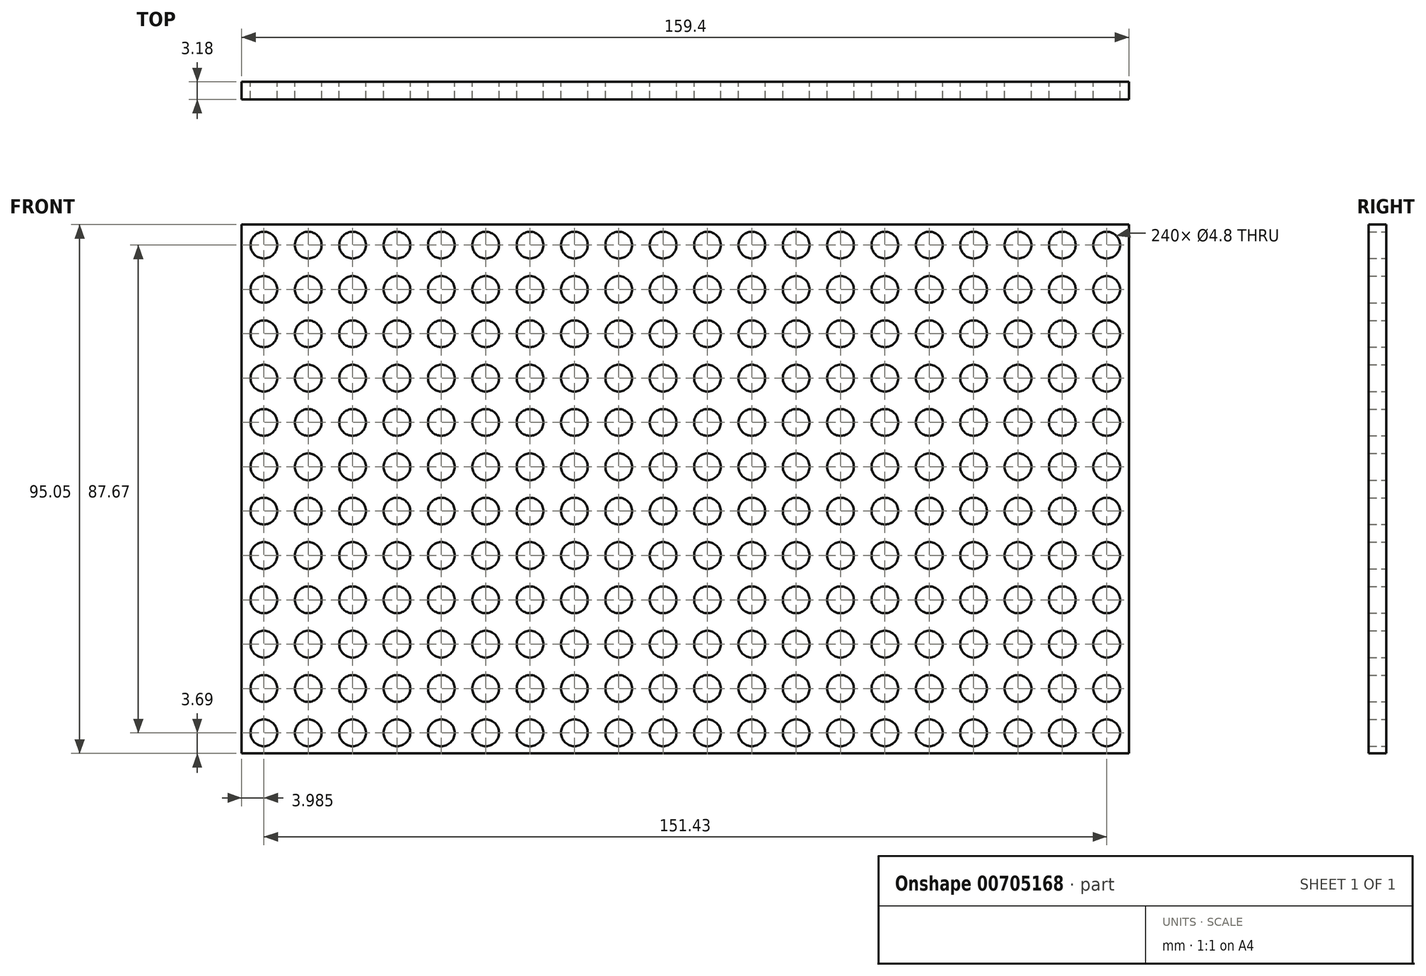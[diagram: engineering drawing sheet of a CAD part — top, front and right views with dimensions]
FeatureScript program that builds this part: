
annotation { "Feature Type Name" : "Feature", "Feature Type Description" : "" }
export const myFeature = defineFeature(function(context is Context, id is Id, definition is map)
    precondition{}
    {
        {
            var Q0;
            Q0=qCreatedBy(makeId("Front.planeOp"),FACE);
            var sketch = newSketch(context, id + "F0", { "sketchPlane" : qUnion([Q0])});
            skLineSegment(sketch, "E0.bottom", {"start": v(0, 0) * mm, "end": v(159.4, 0) * mm});
            skLineSegment(sketch, "E0.top", {"start": v(0, -95.05) * mm, "end": v(159.4, -95.05) * mm});
            skLineSegment(sketch, "E0.left", {"start": v(0, 0) * mm, "end": v(0, -95.05) * mm});
            skLineSegment(sketch, "E0.right", {"start": v(159.4, 0) * mm, "end": v(159.4, -95.05) * mm});
            skCircle(sketch, "E1", {"center": v(3.98, -3.69) * mm, "radius": 2.4 * mm});
            skCircle(sketch, "E2", {"center": v(11.95, -3.69) * mm, "radius": 2.4 * mm});
            skCircle(sketch, "E3.1.0.0", {"center": v(19.92, -3.69) * mm, "radius": 2.4 * mm});
            skCircle(sketch, "E3.2.0.0", {"center": v(27.9, -3.69) * mm, "radius": 2.4 * mm});
            skCircle(sketch, "E3.3.0.0", {"center": v(35.86, -3.69) * mm, "radius": 2.4 * mm});
            skCircle(sketch, "E3.4.0.0", {"center": v(43.83, -3.69) * mm, "radius": 2.4 * mm});
            skCircle(sketch, "E3.5.0.0", {"center": v(51.8, -3.69) * mm, "radius": 2.4 * mm});
            skCircle(sketch, "E3.6.0.0", {"center": v(59.77, -3.69) * mm, "radius": 2.4 * mm});
            skCircle(sketch, "E3.7.0.0", {"center": v(67.74, -3.69) * mm, "radius": 2.4 * mm});
            skCircle(sketch, "E3.8.0.0", {"center": v(75.71, -3.69) * mm, "radius": 2.4 * mm});
            skCircle(sketch, "E3.9.0.0", {"center": v(83.68, -3.69) * mm, "radius": 2.4 * mm});
            skCircle(sketch, "E3.10.0.0", {"center": v(91.65, -3.69) * mm, "radius": 2.4 * mm});
            skCircle(sketch, "E3.11.0.0", {"center": v(99.62, -3.69) * mm, "radius": 2.4 * mm});
            skCircle(sketch, "E3.12.0.0", {"center": v(107.6, -3.69) * mm, "radius": 2.4 * mm});
            skCircle(sketch, "E3.13.0.0", {"center": v(115.56, -3.69) * mm, "radius": 2.4 * mm});
            skCircle(sketch, "E3.14.0.0", {"center": v(123.53, -3.69) * mm, "radius": 2.4 * mm});
            skCircle(sketch, "E3.15.0.0", {"center": v(131.5, -3.69) * mm, "radius": 2.4 * mm});
            skCircle(sketch, "E3.16.0.0", {"center": v(139.47, -3.69) * mm, "radius": 2.4 * mm});
            skCircle(sketch, "E3.17.0.0", {"center": v(147.44, -3.69) * mm, "radius": 2.4 * mm});
            skCircle(sketch, "E3.18.0.0", {"center": v(155.41, -3.69) * mm, "radius": 2.4 * mm});
            skLineSegment(sketch, "E3.direction1", {"start": v(11.95, -3.69) * mm, "end": v(19.92, -3.69) * mm, "construction": true});
            skCircle(sketch, "E4.0.1.0", {"center": v(3.98, -11.66) * mm, "radius": 2.4 * mm});
            skCircle(sketch, "E4.0.1.1", {"center": v(11.95, -11.66) * mm, "radius": 2.4 * mm});
            skCircle(sketch, "E4.0.1.2", {"center": v(19.92, -11.66) * mm, "radius": 2.4 * mm});
            skCircle(sketch, "E4.0.1.3", {"center": v(27.9, -11.66) * mm, "radius": 2.4 * mm});
            skCircle(sketch, "E4.0.1.4", {"center": v(35.86, -11.66) * mm, "radius": 2.4 * mm});
            skCircle(sketch, "E4.0.1.5", {"center": v(43.83, -11.66) * mm, "radius": 2.4 * mm});
            skCircle(sketch, "E4.0.1.6", {"center": v(51.8, -11.66) * mm, "radius": 2.4 * mm});
            skCircle(sketch, "E4.0.1.7", {"center": v(155.41, -11.66) * mm, "radius": 2.4 * mm});
            skCircle(sketch, "E4.0.1.8", {"center": v(147.44, -11.66) * mm, "radius": 2.4 * mm});
            skCircle(sketch, "E4.0.1.9", {"center": v(139.47, -11.66) * mm, "radius": 2.4 * mm});
            skCircle(sketch, "E4.0.1.10", {"center": v(131.5, -11.66) * mm, "radius": 2.4 * mm});
            skCircle(sketch, "E4.0.1.11", {"center": v(123.53, -11.66) * mm, "radius": 2.4 * mm});
            skCircle(sketch, "E4.0.1.12", {"center": v(115.56, -11.66) * mm, "radius": 2.4 * mm});
            skCircle(sketch, "E4.0.1.13", {"center": v(107.6, -11.66) * mm, "radius": 2.4 * mm});
            skCircle(sketch, "E4.0.1.14", {"center": v(99.62, -11.66) * mm, "radius": 2.4 * mm});
            skCircle(sketch, "E4.0.1.15", {"center": v(91.65, -11.66) * mm, "radius": 2.4 * mm});
            skCircle(sketch, "E4.0.1.16", {"center": v(83.68, -11.66) * mm, "radius": 2.4 * mm});
            skCircle(sketch, "E4.0.1.17", {"center": v(75.71, -11.66) * mm, "radius": 2.4 * mm});
            skCircle(sketch, "E4.0.1.18", {"center": v(67.74, -11.66) * mm, "radius": 2.4 * mm});
            skCircle(sketch, "E4.0.1.19", {"center": v(59.77, -11.66) * mm, "radius": 2.4 * mm});
            skCircle(sketch, "E4.0.2.0", {"center": v(3.98, -19.63) * mm, "radius": 2.4 * mm});
            skCircle(sketch, "E4.0.2.1", {"center": v(11.95, -19.63) * mm, "radius": 2.4 * mm});
            skCircle(sketch, "E4.0.2.2", {"center": v(19.92, -19.63) * mm, "radius": 2.4 * mm});
            skCircle(sketch, "E4.0.2.3", {"center": v(27.9, -19.63) * mm, "radius": 2.4 * mm});
            skCircle(sketch, "E4.0.2.4", {"center": v(35.86, -19.63) * mm, "radius": 2.4 * mm});
            skCircle(sketch, "E4.0.2.5", {"center": v(43.83, -19.63) * mm, "radius": 2.4 * mm});
            skCircle(sketch, "E4.0.2.6", {"center": v(51.8, -19.63) * mm, "radius": 2.4 * mm});
            skCircle(sketch, "E4.0.2.7", {"center": v(155.41, -19.63) * mm, "radius": 2.4 * mm});
            skCircle(sketch, "E4.0.2.8", {"center": v(147.44, -19.63) * mm, "radius": 2.4 * mm});
            skCircle(sketch, "E4.0.2.9", {"center": v(139.47, -19.63) * mm, "radius": 2.4 * mm});
            skCircle(sketch, "E4.0.2.10", {"center": v(131.5, -19.63) * mm, "radius": 2.4 * mm});
            skCircle(sketch, "E4.0.2.11", {"center": v(123.53, -19.63) * mm, "radius": 2.4 * mm});
            skCircle(sketch, "E4.0.2.12", {"center": v(115.56, -19.63) * mm, "radius": 2.4 * mm});
            skCircle(sketch, "E4.0.2.13", {"center": v(107.6, -19.63) * mm, "radius": 2.4 * mm});
            skCircle(sketch, "E4.0.2.14", {"center": v(99.62, -19.63) * mm, "radius": 2.4 * mm});
            skCircle(sketch, "E4.0.2.15", {"center": v(91.65, -19.63) * mm, "radius": 2.4 * mm});
            skCircle(sketch, "E4.0.2.16", {"center": v(83.68, -19.63) * mm, "radius": 2.4 * mm});
            skCircle(sketch, "E4.0.2.17", {"center": v(75.71, -19.63) * mm, "radius": 2.4 * mm});
            skCircle(sketch, "E4.0.2.18", {"center": v(67.74, -19.63) * mm, "radius": 2.4 * mm});
            skCircle(sketch, "E4.0.2.19", {"center": v(59.77, -19.63) * mm, "radius": 2.4 * mm});
            skCircle(sketch, "E4.0.3.0", {"center": v(3.98, -27.6) * mm, "radius": 2.4 * mm});
            skCircle(sketch, "E4.0.3.1", {"center": v(11.95, -27.6) * mm, "radius": 2.4 * mm});
            skCircle(sketch, "E4.0.3.2", {"center": v(19.92, -27.6) * mm, "radius": 2.4 * mm});
            skCircle(sketch, "E4.0.3.3", {"center": v(27.9, -27.6) * mm, "radius": 2.4 * mm});
            skCircle(sketch, "E4.0.3.4", {"center": v(35.86, -27.6) * mm, "radius": 2.4 * mm});
            skCircle(sketch, "E4.0.3.5", {"center": v(43.83, -27.6) * mm, "radius": 2.4 * mm});
            skCircle(sketch, "E4.0.3.6", {"center": v(51.8, -27.6) * mm, "radius": 2.4 * mm});
            skCircle(sketch, "E4.0.3.7", {"center": v(155.41, -27.6) * mm, "radius": 2.4 * mm});
            skCircle(sketch, "E4.0.3.8", {"center": v(147.44, -27.6) * mm, "radius": 2.4 * mm});
            skCircle(sketch, "E4.0.3.9", {"center": v(139.47, -27.6) * mm, "radius": 2.4 * mm});
            skCircle(sketch, "E4.0.3.10", {"center": v(131.5, -27.6) * mm, "radius": 2.4 * mm});
            skCircle(sketch, "E4.0.3.11", {"center": v(123.53, -27.6) * mm, "radius": 2.4 * mm});
            skCircle(sketch, "E4.0.3.12", {"center": v(115.56, -27.6) * mm, "radius": 2.4 * mm});
            skCircle(sketch, "E4.0.3.13", {"center": v(107.6, -27.6) * mm, "radius": 2.4 * mm});
            skCircle(sketch, "E4.0.3.14", {"center": v(99.62, -27.6) * mm, "radius": 2.4 * mm});
            skCircle(sketch, "E4.0.3.15", {"center": v(91.65, -27.6) * mm, "radius": 2.4 * mm});
            skCircle(sketch, "E4.0.3.16", {"center": v(83.68, -27.6) * mm, "radius": 2.4 * mm});
            skCircle(sketch, "E4.0.3.17", {"center": v(75.71, -27.6) * mm, "radius": 2.4 * mm});
            skCircle(sketch, "E4.0.3.18", {"center": v(67.74, -27.6) * mm, "radius": 2.4 * mm});
            skCircle(sketch, "E4.0.3.19", {"center": v(59.77, -27.6) * mm, "radius": 2.4 * mm});
            skCircle(sketch, "E4.0.4.0", {"center": v(3.98, -35.57) * mm, "radius": 2.4 * mm});
            skCircle(sketch, "E4.0.4.1", {"center": v(11.95, -35.57) * mm, "radius": 2.4 * mm});
            skCircle(sketch, "E4.0.4.2", {"center": v(19.92, -35.57) * mm, "radius": 2.4 * mm});
            skCircle(sketch, "E4.0.4.3", {"center": v(27.9, -35.57) * mm, "radius": 2.4 * mm});
            skCircle(sketch, "E4.0.4.4", {"center": v(35.86, -35.57) * mm, "radius": 2.4 * mm});
            skCircle(sketch, "E4.0.4.5", {"center": v(43.83, -35.57) * mm, "radius": 2.4 * mm});
            skCircle(sketch, "E4.0.4.6", {"center": v(51.8, -35.57) * mm, "radius": 2.4 * mm});
            skCircle(sketch, "E4.0.4.7", {"center": v(155.41, -35.57) * mm, "radius": 2.4 * mm});
            skCircle(sketch, "E4.0.4.8", {"center": v(147.44, -35.57) * mm, "radius": 2.4 * mm});
            skCircle(sketch, "E4.0.4.9", {"center": v(139.47, -35.57) * mm, "radius": 2.4 * mm});
            skCircle(sketch, "E4.0.4.10", {"center": v(131.5, -35.57) * mm, "radius": 2.4 * mm});
            skCircle(sketch, "E4.0.4.11", {"center": v(123.53, -35.57) * mm, "radius": 2.4 * mm});
            skCircle(sketch, "E4.0.4.12", {"center": v(115.56, -35.57) * mm, "radius": 2.4 * mm});
            skCircle(sketch, "E4.0.4.13", {"center": v(107.6, -35.57) * mm, "radius": 2.4 * mm});
            skCircle(sketch, "E4.0.4.14", {"center": v(99.62, -35.57) * mm, "radius": 2.4 * mm});
            skCircle(sketch, "E4.0.4.15", {"center": v(91.65, -35.57) * mm, "radius": 2.4 * mm});
            skCircle(sketch, "E4.0.4.16", {"center": v(83.68, -35.57) * mm, "radius": 2.4 * mm});
            skCircle(sketch, "E4.0.4.17", {"center": v(75.71, -35.57) * mm, "radius": 2.4 * mm});
            skCircle(sketch, "E4.0.4.18", {"center": v(67.74, -35.57) * mm, "radius": 2.4 * mm});
            skCircle(sketch, "E4.0.4.19", {"center": v(59.77, -35.57) * mm, "radius": 2.4 * mm});
            skCircle(sketch, "E4.0.5.0", {"center": v(3.98, -43.54) * mm, "radius": 2.4 * mm});
            skCircle(sketch, "E4.0.5.1", {"center": v(11.95, -43.54) * mm, "radius": 2.4 * mm});
            skCircle(sketch, "E4.0.5.2", {"center": v(19.92, -43.54) * mm, "radius": 2.4 * mm});
            skCircle(sketch, "E4.0.5.3", {"center": v(27.9, -43.54) * mm, "radius": 2.4 * mm});
            skCircle(sketch, "E4.0.5.4", {"center": v(35.86, -43.54) * mm, "radius": 2.4 * mm});
            skCircle(sketch, "E4.0.5.5", {"center": v(43.83, -43.54) * mm, "radius": 2.4 * mm});
            skCircle(sketch, "E4.0.5.6", {"center": v(51.8, -43.54) * mm, "radius": 2.4 * mm});
            skCircle(sketch, "E4.0.5.7", {"center": v(155.41, -43.54) * mm, "radius": 2.4 * mm});
            skCircle(sketch, "E4.0.5.8", {"center": v(147.44, -43.54) * mm, "radius": 2.4 * mm});
            skCircle(sketch, "E4.0.5.9", {"center": v(139.47, -43.54) * mm, "radius": 2.4 * mm});
            skCircle(sketch, "E4.0.5.10", {"center": v(131.5, -43.54) * mm, "radius": 2.4 * mm});
            skCircle(sketch, "E4.0.5.11", {"center": v(123.53, -43.54) * mm, "radius": 2.4 * mm});
            skCircle(sketch, "E4.0.5.12", {"center": v(115.56, -43.54) * mm, "radius": 2.4 * mm});
            skCircle(sketch, "E4.0.5.13", {"center": v(107.6, -43.54) * mm, "radius": 2.4 * mm});
            skCircle(sketch, "E4.0.5.14", {"center": v(99.62, -43.54) * mm, "radius": 2.4 * mm});
            skCircle(sketch, "E4.0.5.15", {"center": v(91.65, -43.54) * mm, "radius": 2.4 * mm});
            skCircle(sketch, "E4.0.5.16", {"center": v(83.68, -43.54) * mm, "radius": 2.4 * mm});
            skCircle(sketch, "E4.0.5.17", {"center": v(75.71, -43.54) * mm, "radius": 2.4 * mm});
            skCircle(sketch, "E4.0.5.18", {"center": v(67.74, -43.54) * mm, "radius": 2.4 * mm});
            skCircle(sketch, "E4.0.5.19", {"center": v(59.77, -43.54) * mm, "radius": 2.4 * mm});
            skCircle(sketch, "E4.0.6.0", {"center": v(3.98, -51.5) * mm, "radius": 2.4 * mm});
            skCircle(sketch, "E4.0.6.1", {"center": v(11.95, -51.5) * mm, "radius": 2.4 * mm});
            skCircle(sketch, "E4.0.6.2", {"center": v(19.92, -51.5) * mm, "radius": 2.4 * mm});
            skCircle(sketch, "E4.0.6.3", {"center": v(27.9, -51.5) * mm, "radius": 2.4 * mm});
            skCircle(sketch, "E4.0.6.4", {"center": v(35.86, -51.5) * mm, "radius": 2.4 * mm});
            skCircle(sketch, "E4.0.6.5", {"center": v(43.83, -51.5) * mm, "radius": 2.4 * mm});
            skCircle(sketch, "E4.0.6.6", {"center": v(51.8, -51.5) * mm, "radius": 2.4 * mm});
            skCircle(sketch, "E4.0.6.7", {"center": v(155.41, -51.5) * mm, "radius": 2.4 * mm});
            skCircle(sketch, "E4.0.6.8", {"center": v(147.44, -51.5) * mm, "radius": 2.4 * mm});
            skCircle(sketch, "E4.0.6.9", {"center": v(139.47, -51.5) * mm, "radius": 2.4 * mm});
            skCircle(sketch, "E4.0.6.10", {"center": v(131.5, -51.5) * mm, "radius": 2.4 * mm});
            skCircle(sketch, "E4.0.6.11", {"center": v(123.53, -51.5) * mm, "radius": 2.4 * mm});
            skCircle(sketch, "E4.0.6.12", {"center": v(115.56, -51.5) * mm, "radius": 2.4 * mm});
            skCircle(sketch, "E4.0.6.13", {"center": v(107.6, -51.5) * mm, "radius": 2.4 * mm});
            skCircle(sketch, "E4.0.6.14", {"center": v(99.62, -51.5) * mm, "radius": 2.4 * mm});
            skCircle(sketch, "E4.0.6.15", {"center": v(91.65, -51.5) * mm, "radius": 2.4 * mm});
            skCircle(sketch, "E4.0.6.16", {"center": v(83.68, -51.5) * mm, "radius": 2.4 * mm});
            skCircle(sketch, "E4.0.6.17", {"center": v(75.71, -51.5) * mm, "radius": 2.4 * mm});
            skCircle(sketch, "E4.0.6.18", {"center": v(67.74, -51.5) * mm, "radius": 2.4 * mm});
            skCircle(sketch, "E4.0.6.19", {"center": v(59.77, -51.5) * mm, "radius": 2.4 * mm});
            skCircle(sketch, "E4.0.7.0", {"center": v(3.98, -59.48) * mm, "radius": 2.4 * mm});
            skCircle(sketch, "E4.0.7.1", {"center": v(11.95, -59.48) * mm, "radius": 2.4 * mm});
            skCircle(sketch, "E4.0.7.2", {"center": v(19.92, -59.48) * mm, "radius": 2.4 * mm});
            skCircle(sketch, "E4.0.7.3", {"center": v(27.9, -59.48) * mm, "radius": 2.4 * mm});
            skCircle(sketch, "E4.0.7.4", {"center": v(35.86, -59.48) * mm, "radius": 2.4 * mm});
            skCircle(sketch, "E4.0.7.5", {"center": v(43.83, -59.48) * mm, "radius": 2.4 * mm});
            skCircle(sketch, "E4.0.7.6", {"center": v(51.8, -59.48) * mm, "radius": 2.4 * mm});
            skCircle(sketch, "E4.0.7.7", {"center": v(155.41, -59.48) * mm, "radius": 2.4 * mm});
            skCircle(sketch, "E4.0.7.8", {"center": v(147.44, -59.48) * mm, "radius": 2.4 * mm});
            skCircle(sketch, "E4.0.7.9", {"center": v(139.47, -59.48) * mm, "radius": 2.4 * mm});
            skCircle(sketch, "E4.0.7.10", {"center": v(131.5, -59.48) * mm, "radius": 2.4 * mm});
            skCircle(sketch, "E4.0.7.11", {"center": v(123.53, -59.48) * mm, "radius": 2.4 * mm});
            skCircle(sketch, "E4.0.7.12", {"center": v(115.56, -59.48) * mm, "radius": 2.4 * mm});
            skCircle(sketch, "E4.0.7.13", {"center": v(107.6, -59.48) * mm, "radius": 2.4 * mm});
            skCircle(sketch, "E4.0.7.14", {"center": v(99.62, -59.48) * mm, "radius": 2.4 * mm});
            skCircle(sketch, "E4.0.7.15", {"center": v(91.65, -59.48) * mm, "radius": 2.4 * mm});
            skCircle(sketch, "E4.0.7.16", {"center": v(83.68, -59.48) * mm, "radius": 2.4 * mm});
            skCircle(sketch, "E4.0.7.17", {"center": v(75.71, -59.48) * mm, "radius": 2.4 * mm});
            skCircle(sketch, "E4.0.7.18", {"center": v(67.74, -59.48) * mm, "radius": 2.4 * mm});
            skCircle(sketch, "E4.0.7.19", {"center": v(59.77, -59.48) * mm, "radius": 2.4 * mm});
            skCircle(sketch, "E4.0.8.0", {"center": v(3.98, -67.45) * mm, "radius": 2.4 * mm});
            skCircle(sketch, "E4.0.8.1", {"center": v(11.95, -67.45) * mm, "radius": 2.4 * mm});
            skCircle(sketch, "E4.0.8.2", {"center": v(19.92, -67.45) * mm, "radius": 2.4 * mm});
            skCircle(sketch, "E4.0.8.3", {"center": v(27.9, -67.45) * mm, "radius": 2.4 * mm});
            skCircle(sketch, "E4.0.8.4", {"center": v(35.86, -67.45) * mm, "radius": 2.4 * mm});
            skCircle(sketch, "E4.0.8.5", {"center": v(43.83, -67.45) * mm, "radius": 2.4 * mm});
            skCircle(sketch, "E4.0.8.6", {"center": v(51.8, -67.45) * mm, "radius": 2.4 * mm});
            skCircle(sketch, "E4.0.8.7", {"center": v(155.41, -67.45) * mm, "radius": 2.4 * mm});
            skCircle(sketch, "E4.0.8.8", {"center": v(147.44, -67.45) * mm, "radius": 2.4 * mm});
            skCircle(sketch, "E4.0.8.9", {"center": v(139.47, -67.45) * mm, "radius": 2.4 * mm});
            skCircle(sketch, "E4.0.8.10", {"center": v(131.5, -67.45) * mm, "radius": 2.4 * mm});
            skCircle(sketch, "E4.0.8.11", {"center": v(123.53, -67.45) * mm, "radius": 2.4 * mm});
            skCircle(sketch, "E4.0.8.12", {"center": v(115.56, -67.45) * mm, "radius": 2.4 * mm});
            skCircle(sketch, "E4.0.8.13", {"center": v(107.6, -67.45) * mm, "radius": 2.4 * mm});
            skCircle(sketch, "E4.0.8.14", {"center": v(99.62, -67.45) * mm, "radius": 2.4 * mm});
            skCircle(sketch, "E4.0.8.15", {"center": v(91.65, -67.45) * mm, "radius": 2.4 * mm});
            skCircle(sketch, "E4.0.8.16", {"center": v(83.68, -67.45) * mm, "radius": 2.4 * mm});
            skCircle(sketch, "E4.0.8.17", {"center": v(75.71, -67.45) * mm, "radius": 2.4 * mm});
            skCircle(sketch, "E4.0.8.18", {"center": v(67.74, -67.45) * mm, "radius": 2.4 * mm});
            skCircle(sketch, "E4.0.8.19", {"center": v(59.77, -67.45) * mm, "radius": 2.4 * mm});
            skCircle(sketch, "E4.0.9.0", {"center": v(3.98, -75.42) * mm, "radius": 2.4 * mm});
            skCircle(sketch, "E4.0.9.1", {"center": v(11.95, -75.42) * mm, "radius": 2.4 * mm});
            skCircle(sketch, "E4.0.9.2", {"center": v(19.92, -75.42) * mm, "radius": 2.4 * mm});
            skCircle(sketch, "E4.0.9.3", {"center": v(27.9, -75.42) * mm, "radius": 2.4 * mm});
            skCircle(sketch, "E4.0.9.4", {"center": v(35.86, -75.42) * mm, "radius": 2.4 * mm});
            skCircle(sketch, "E4.0.9.5", {"center": v(43.83, -75.42) * mm, "radius": 2.4 * mm});
            skCircle(sketch, "E4.0.9.6", {"center": v(51.8, -75.42) * mm, "radius": 2.4 * mm});
            skCircle(sketch, "E4.0.9.7", {"center": v(155.41, -75.42) * mm, "radius": 2.4 * mm});
            skCircle(sketch, "E4.0.9.8", {"center": v(147.44, -75.42) * mm, "radius": 2.4 * mm});
            skCircle(sketch, "E4.0.9.9", {"center": v(139.47, -75.42) * mm, "radius": 2.4 * mm});
            skCircle(sketch, "E4.0.9.10", {"center": v(131.5, -75.42) * mm, "radius": 2.4 * mm});
            skCircle(sketch, "E4.0.9.11", {"center": v(123.53, -75.42) * mm, "radius": 2.4 * mm});
            skCircle(sketch, "E4.0.9.12", {"center": v(115.56, -75.42) * mm, "radius": 2.4 * mm});
            skCircle(sketch, "E4.0.9.13", {"center": v(107.6, -75.42) * mm, "radius": 2.4 * mm});
            skCircle(sketch, "E4.0.9.14", {"center": v(99.62, -75.42) * mm, "radius": 2.4 * mm});
            skCircle(sketch, "E4.0.9.15", {"center": v(91.65, -75.42) * mm, "radius": 2.4 * mm});
            skCircle(sketch, "E4.0.9.16", {"center": v(83.68, -75.42) * mm, "radius": 2.4 * mm});
            skCircle(sketch, "E4.0.9.17", {"center": v(75.71, -75.42) * mm, "radius": 2.4 * mm});
            skCircle(sketch, "E4.0.9.18", {"center": v(67.74, -75.42) * mm, "radius": 2.4 * mm});
            skCircle(sketch, "E4.0.9.19", {"center": v(59.77, -75.42) * mm, "radius": 2.4 * mm});
            skCircle(sketch, "E4.0.10.0", {"center": v(3.98, -83.39) * mm, "radius": 2.4 * mm});
            skCircle(sketch, "E4.0.10.1", {"center": v(11.95, -83.39) * mm, "radius": 2.4 * mm});
            skCircle(sketch, "E4.0.10.2", {"center": v(19.92, -83.39) * mm, "radius": 2.4 * mm});
            skCircle(sketch, "E4.0.10.3", {"center": v(27.9, -83.39) * mm, "radius": 2.4 * mm});
            skCircle(sketch, "E4.0.10.4", {"center": v(35.86, -83.39) * mm, "radius": 2.4 * mm});
            skCircle(sketch, "E4.0.10.5", {"center": v(43.83, -83.39) * mm, "radius": 2.4 * mm});
            skCircle(sketch, "E4.0.10.6", {"center": v(51.8, -83.39) * mm, "radius": 2.4 * mm});
            skCircle(sketch, "E4.0.10.7", {"center": v(155.41, -83.39) * mm, "radius": 2.4 * mm});
            skCircle(sketch, "E4.0.10.8", {"center": v(147.44, -83.39) * mm, "radius": 2.4 * mm});
            skCircle(sketch, "E4.0.10.9", {"center": v(139.47, -83.39) * mm, "radius": 2.4 * mm});
            skCircle(sketch, "E4.0.10.10", {"center": v(131.5, -83.39) * mm, "radius": 2.4 * mm});
            skCircle(sketch, "E4.0.10.11", {"center": v(123.53, -83.39) * mm, "radius": 2.4 * mm});
            skCircle(sketch, "E4.0.10.12", {"center": v(115.56, -83.39) * mm, "radius": 2.4 * mm});
            skCircle(sketch, "E4.0.10.13", {"center": v(107.6, -83.39) * mm, "radius": 2.4 * mm});
            skCircle(sketch, "E4.0.10.14", {"center": v(99.62, -83.39) * mm, "radius": 2.4 * mm});
            skCircle(sketch, "E4.0.10.15", {"center": v(91.65, -83.39) * mm, "radius": 2.4 * mm});
            skCircle(sketch, "E4.0.10.16", {"center": v(83.68, -83.39) * mm, "radius": 2.4 * mm});
            skCircle(sketch, "E4.0.10.17", {"center": v(75.71, -83.39) * mm, "radius": 2.4 * mm});
            skCircle(sketch, "E4.0.10.18", {"center": v(67.74, -83.39) * mm, "radius": 2.4 * mm});
            skCircle(sketch, "E4.0.10.19", {"center": v(59.77, -83.39) * mm, "radius": 2.4 * mm});
            skCircle(sketch, "E4.0.11.0", {"center": v(3.98, -91.36) * mm, "radius": 2.4 * mm});
            skCircle(sketch, "E4.0.11.1", {"center": v(11.95, -91.36) * mm, "radius": 2.4 * mm});
            skCircle(sketch, "E4.0.11.2", {"center": v(19.92, -91.36) * mm, "radius": 2.4 * mm});
            skCircle(sketch, "E4.0.11.3", {"center": v(27.9, -91.36) * mm, "radius": 2.4 * mm});
            skCircle(sketch, "E4.0.11.4", {"center": v(35.86, -91.36) * mm, "radius": 2.4 * mm});
            skCircle(sketch, "E4.0.11.5", {"center": v(43.83, -91.36) * mm, "radius": 2.4 * mm});
            skCircle(sketch, "E4.0.11.6", {"center": v(51.8, -91.36) * mm, "radius": 2.4 * mm});
            skCircle(sketch, "E4.0.11.7", {"center": v(155.41, -91.36) * mm, "radius": 2.4 * mm});
            skCircle(sketch, "E4.0.11.8", {"center": v(147.44, -91.36) * mm, "radius": 2.4 * mm});
            skCircle(sketch, "E4.0.11.9", {"center": v(139.47, -91.36) * mm, "radius": 2.4 * mm});
            skCircle(sketch, "E4.0.11.10", {"center": v(131.5, -91.36) * mm, "radius": 2.4 * mm});
            skCircle(sketch, "E4.0.11.11", {"center": v(123.53, -91.36) * mm, "radius": 2.4 * mm});
            skCircle(sketch, "E4.0.11.12", {"center": v(115.56, -91.36) * mm, "radius": 2.4 * mm});
            skCircle(sketch, "E4.0.11.13", {"center": v(107.6, -91.36) * mm, "radius": 2.4 * mm});
            skCircle(sketch, "E4.0.11.14", {"center": v(99.62, -91.36) * mm, "radius": 2.4 * mm});
            skCircle(sketch, "E4.0.11.15", {"center": v(91.65, -91.36) * mm, "radius": 2.4 * mm});
            skCircle(sketch, "E4.0.11.16", {"center": v(83.68, -91.36) * mm, "radius": 2.4 * mm});
            skCircle(sketch, "E4.0.11.17", {"center": v(75.71, -91.36) * mm, "radius": 2.4 * mm});
            skCircle(sketch, "E4.0.11.18", {"center": v(67.74, -91.36) * mm, "radius": 2.4 * mm});
            skCircle(sketch, "E4.0.11.19", {"center": v(59.77, -91.36) * mm, "radius": 2.4 * mm});
            skLineSegment(sketch, "E4.direction1", {"start": v(3.98, -3.69) * mm, "end": v(29.38, -3.69) * mm, "construction": true});
            skLineSegment(sketch, "E4.direction2", {"start": v(3.98, -3.69) * mm, "end": v(3.98, -11.66) * mm, "construction": true});
            skSolve(sketch);
        }
        {
            var Q0;
            Q0=makeQuery(id+"F0.imprint","IMPRINT",FACE,{"disambiguationData":[TD([[makeQuery(id+"F0.imprint","IMPRINT",EDGE,{"derivedFrom":sQuery(id+"F0.wireOp",EDGE,"E0.bottom")}),-1.0]])]});
            extrude(context, id + "F1", {"entities" : qUnion([Q0]), "depth" : 3.17 * mm, "offsetDistance" : 25.4 * mm});
        }
    });
